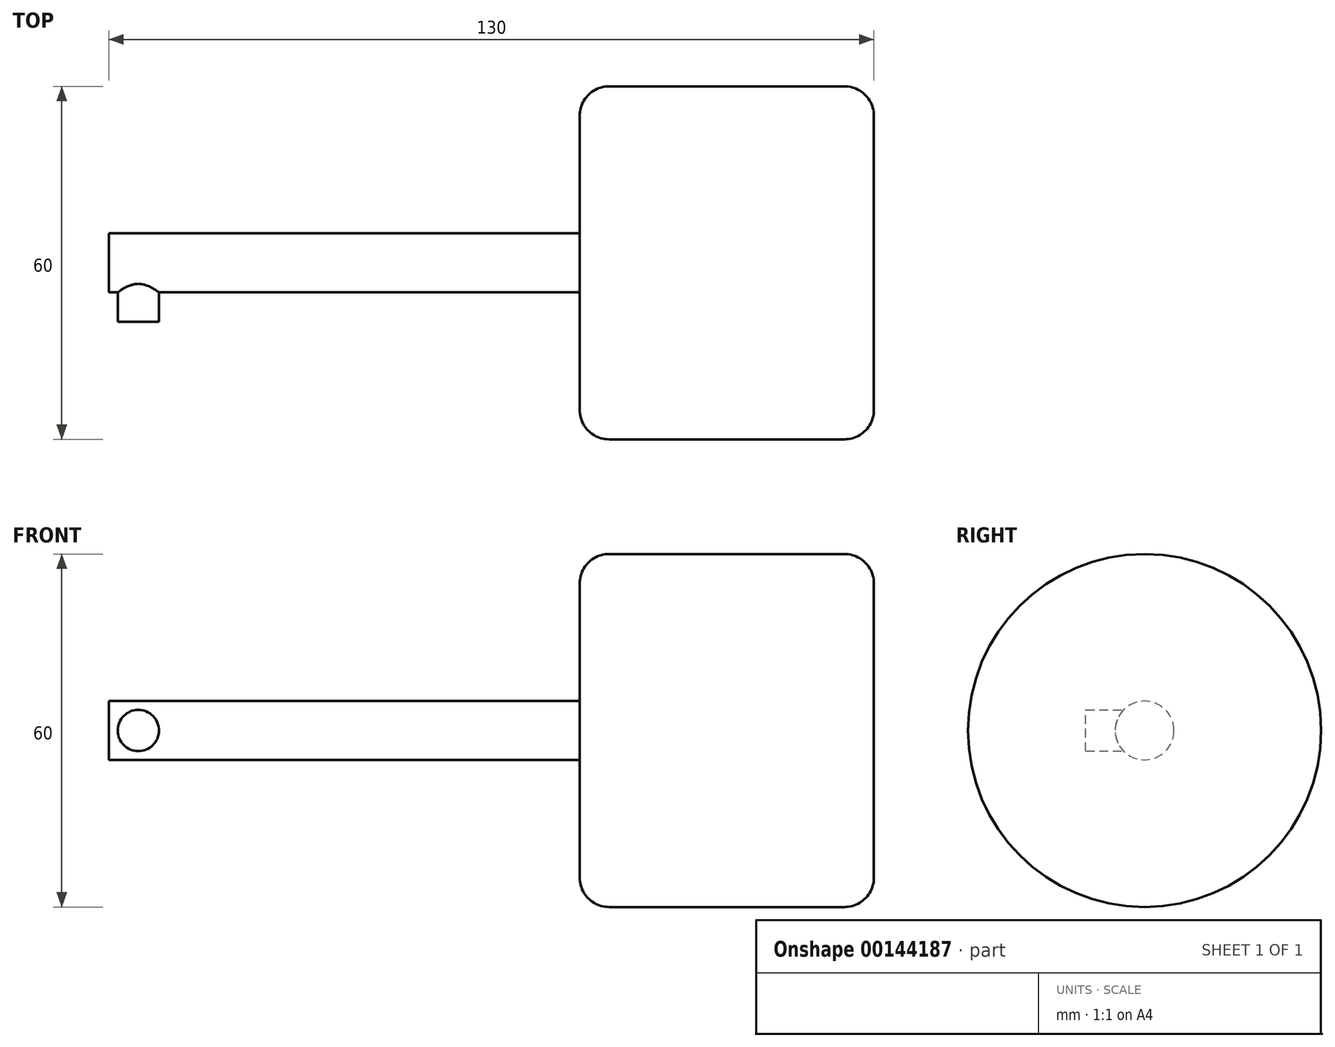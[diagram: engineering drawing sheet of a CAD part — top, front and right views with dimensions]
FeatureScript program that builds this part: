
annotation { "Feature Type Name" : "Feature", "Feature Type Description" : "" }
export const myFeature = defineFeature(function(context is Context, id is Id, definition is map)
    precondition{}
    {
        {
            var Q0;
            Q0=qCreatedBy(makeId("Right.planeOp"),FACE);
            var sketch = newSketch(context, id + "F0", { "sketchPlane" : qUnion([Q0])});
            skCircle(sketch, "E0", {"center": v(0, 0) * mm, "radius": 30 * mm});
            skSolve(sketch);
        }
        {
            var Q0;
            Q0 = qSketchRegion(id + "F0", true);
            extrude(context, id + "F1", {"entities" : qUnion([Q0]), "depth" : 50 * mm});
        }
        {
            var Q0;
            Q0=qCreatedBy(makeId("Right.planeOp"),FACE);
            var sketch = newSketch(context, id + "F2", { "sketchPlane" : qUnion([Q0])});
            skCircle(sketch, "E1", {"center": v(0, 0) * mm, "radius": 5 * mm});
            skSolve(sketch);
        }
        {
            var Q0;
            Q0 = qSketchRegion(id + "F2", true);
            extrude(context, id + "F3", {"entities" : qUnion([Q0]), "operationType" : NewBodyOperationType.ADD, "oppositeDirection" : true, "depth" : 80 * mm});
        }
        {
            var Q0;
            Q0=qCreatedBy(makeId("Front.planeOp"),FACE);
            var sketch = newSketch(context, id + "F4", { "sketchPlane" : qUnion([Q0])});
            skCircle(sketch, "E2", {"center": v(-75, 0) * mm, "radius": 3.5 * mm});
            skSolve(sketch);
        }
        {
            var Q0;
            Q0 = qSketchRegion(id + "F4", true);
            extrude(context, id + "F5", {"entities" : qUnion([Q0]), "operationType" : NewBodyOperationType.ADD, "depth" : 10 * mm});
        }
        {
            var Q0;
            Q0=makeQuery(id+"F1.opExtrude","CAP_EDGE",EDGE,{"disambiguationData":[OSD([sQuery(id+"F0.wireOp",EDGE,"E0")])],"isStart":false});
            var Q1;
            Q1=makeQuery(id+"F1.opExtrude","CAP_EDGE",EDGE,{"disambiguationData":[OSD([sQuery(id+"F0.wireOp",EDGE,"E0")])],"isStart":true});
            fillet(context, id + "F6", {"entities" : qUnion([Q0, Q1]), "radius" : 5 * mm, "tangentPropagation" : true, "allowEdgeOverflow" : false});
        }
    });
